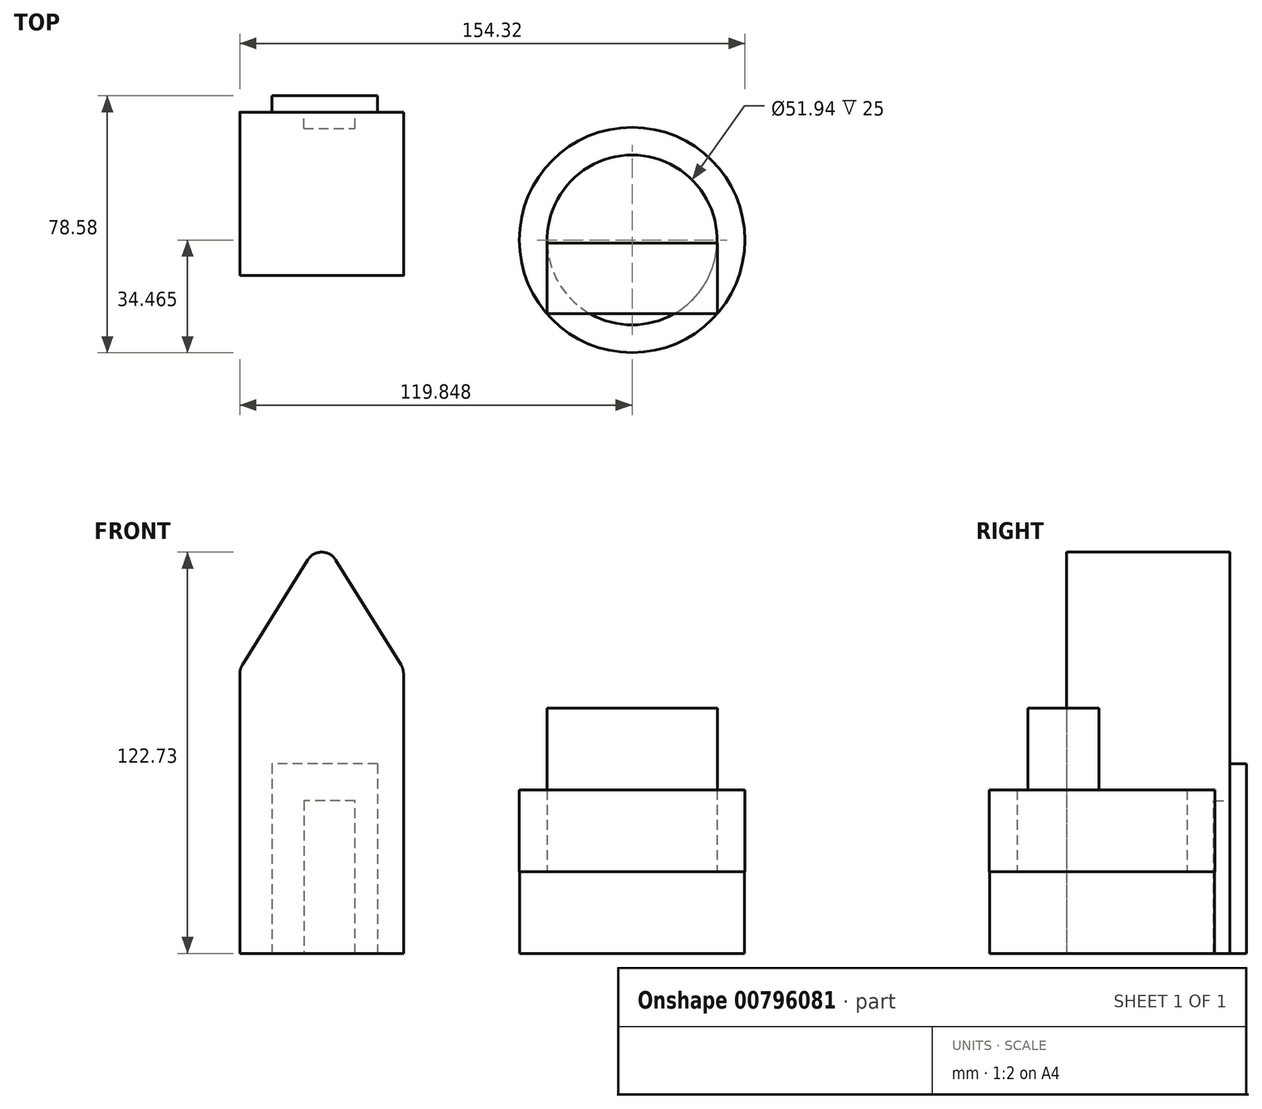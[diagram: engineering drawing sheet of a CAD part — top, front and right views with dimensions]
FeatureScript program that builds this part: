
annotation { "Feature Type Name" : "Feature", "Feature Type Description" : "" }
export const myFeature = defineFeature(function(context is Context, id is Id, definition is map)
    precondition{}
    {
        {
            var Q0;
            Q0=qCreatedBy(makeId("Top.planeOp"),FACE);
            var sketch = newSketch(context, id + "F0", { "sketchPlane" : qUnion([Q0])});
            skPoint(sketch, "E0.middle", {"position": v(0, 0) * mm});
            skLineSegment(sketch, "E1.bottom", {"start": v(-19.52, 23.08) * mm, "end": v(30.48, 23.08) * mm});
            skLineSegment(sketch, "E1.top", {"start": v(-19.52, -26.92) * mm, "end": v(30.48, -26.92) * mm});
            skLineSegment(sketch, "E1.left", {"start": v(-19.52, 23.08) * mm, "end": v(-19.52, -26.92) * mm});
            skLineSegment(sketch, "E1.right", {"start": v(30.48, 23.08) * mm, "end": v(30.48, -26.92) * mm});
            skSolve(sketch);
        }
        {
            var Q0;
            Q0 = qSketchRegion(id + "F0", true);
            extrude(context, id + "F1", {"entities" : qUnion([Q0]), "depth" : 87 * mm, "offsetDistance" : 25 * mm});
        }
        {
            var Q0;
            Q0=makeQuery(id+"F1.opExtrude","SWEPT_FACE",FACE,{"disambiguationData":[OSD([sQuery(id+"F0.wireOp",EDGE,"E1.bottom")])]});
            var sketch = newSketch(context, id + "F2", { "sketchPlane" : qUnion([Q0])});
            skLineSegment(sketch, "E2", {"start": v(-30.48, 87) * mm, "end": v(-5.48, 127.2) * mm});
            skPoint(sketch, "E2.endSnap0", {"position": v(-5.48, 0) * mm});
            skLineSegment(sketch, "E3", {"start": v(-5.48, 127.2) * mm, "end": v(19.52, 87) * mm});
            skLineSegment(sketch, "E4", {"start": v(19.52, 87) * mm, "end": v(-30.48, 87) * mm});
            skSolve(sketch);
        }
        {
            var Q0;
            Q0 = qSketchRegion(id + "F2", true);
            extrude(context, id + "F3", {"entities" : qUnion([Q0]), "operationType" : NewBodyOperationType.ADD, "oppositeDirection" : true, "depth" : 50 * mm, "offsetDistance" : 25 * mm});
        }
        {
            var Q0;
            Q0=makeQuery(id+"F3.boolean.opBoolean","MERGE",FACE,{"derivedFrom":[makeQuery(id+"F1.opExtrude","SWEPT_FACE",FACE,{"disambiguationData":[OSD([sQuery(id+"F0.wireOp",EDGE,"E1.bottom")])]}),makeQuery(id+"F3.opExtrude","CAP_FACE",FACE,{"disambiguationData":[OSD([sQuery(id+"F2.wireOp",EDGE,"E2"),sQuery(id+"F2.wireOp",EDGE,"E3"),sQuery(id+"F2.wireOp",EDGE,"E4")])],"isStart":true})]});
            var sketch = newSketch(context, id + "F4", { "sketchPlane" : qUnion([Q0])});
            skLineSegment(sketch, "E5", {"start": v(-15.66, 0) * mm, "end": v(-15.66, 46.7) * mm});
            skLineSegment(sketch, "E6", {"start": v(-15.66, 46.7) * mm, "end": v(0, 46.7) * mm});
            skLineSegment(sketch, "E7", {"start": v(0, 46.7) * mm, "end": v(0, 0) * mm});
            skLineSegment(sketch, "E8", {"start": v(0, 0) * mm, "end": v(-15.66, 0) * mm});
            skSolve(sketch);
        }
        {
            var Q0;
            Q0 = qSketchRegion(id + "F4", true);
            extrude(context, id + "F5", {"entities" : qUnion([Q0]), "operationType" : NewBodyOperationType.REMOVE, "oppositeDirection" : true, "depth" : 5 * mm, "offsetDistance" : 25 * mm});
        }
        {
            var Q0;
            Q0=makeQuery(id+"F3.boolean.opBoolean","MERGE",FACE,{"derivedFrom":[makeQuery(id+"F1.opExtrude","SWEPT_FACE",FACE,{"disambiguationData":[OSD([sQuery(id+"F0.wireOp",EDGE,"E1.bottom")])]}),makeQuery(id+"F3.opExtrude","CAP_FACE",FACE,{"disambiguationData":[OSD([sQuery(id+"F2.wireOp",EDGE,"E2"),sQuery(id+"F2.wireOp",EDGE,"E3"),sQuery(id+"F2.wireOp",EDGE,"E4")])],"isStart":true})]});
            var sketch = newSketch(context, id + "F6", { "sketchPlane" : qUnion([Q0])});
            skLineSegment(sketch, "E9.bottom", {"start": v(-22.6, 57.96) * mm, "end": v(9.76, 57.96) * mm});
            skLineSegment(sketch, "E9.top", {"start": v(-22.6, 0) * mm, "end": v(9.76, 0) * mm});
            skLineSegment(sketch, "E9.left", {"start": v(-22.6, 57.96) * mm, "end": v(-22.6, 0) * mm});
            skLineSegment(sketch, "E9.right", {"start": v(9.76, 57.96) * mm, "end": v(9.76, 0) * mm});
            skSolve(sketch);
        }
        {
            var Q0;
            Q0 = qSketchRegion(id + "F6", true);
            extrude(context, id + "F7", {"entities" : qUnion([Q0]), "operationType" : NewBodyOperationType.ADD, "depth" : 5 * mm, "offsetDistance" : 25 * mm});
        }
        {
            var Q0;
            Q0=makeQuery(id+"F3.opExtrude","SWEPT_EDGE",EDGE,{"disambiguationData":[OSD([sQuery(id+"F2.wireOp",EDGE,"E2"),sQuery(id+"F2.wireOp",EDGE,"E3")])]});
            var Q1;
            {var subQ0=sQuery(id+"F0.wireOp",EDGE,"E1.right");Q1=makeQuery(id+"F3.boolean.opBoolean","MERGE",EDGE,{"derivedFrom":[makeQuery(id+"F1.opExtrude","CAP_EDGE",EDGE,{"disambiguationData":[OSD([subQ0])],"isStart":false}),makeQuery(id+"F3.opExtrude","SWEPT_EDGE",EDGE,{"disambiguationData":[OSD([sQuery(id+"F0.wireOp",EDGE,"E1.bottom"),subQ0,sQuery(id+"F2.wireOp",EDGE,"E2"),sQuery(id+"F2.wireOp",EDGE,"E4")])]})]});}
            var Q2;
            {var subQ0=sQuery(id+"F0.wireOp",EDGE,"E1.left");Q2=makeQuery(id+"F3.boolean.opBoolean","MERGE",EDGE,{"derivedFrom":[makeQuery(id+"F1.opExtrude","CAP_EDGE",EDGE,{"disambiguationData":[OSD([subQ0])],"isStart":false}),makeQuery(id+"F3.opExtrude","SWEPT_EDGE",EDGE,{"disambiguationData":[OSD([sQuery(id+"F0.wireOp",EDGE,"E1.bottom"),subQ0,sQuery(id+"F2.wireOp",EDGE,"E3"),sQuery(id+"F2.wireOp",EDGE,"E4")])]})]});}
            fillet(context, id + "F8", {"entities" : qUnion([Q0, Q1, Q2]), "radius" : 5 * mm, "tangentPropagation" : true, "allowEdgeOverflow" : false});
        }
        {
            var Q0;
            Q0=qCreatedBy(makeId("Top.planeOp"),FACE);
            var sketch = newSketch(context, id + "F9", { "sketchPlane" : qUnion([Q0])});
            skCircle(sketch, "E10", {"center": v(100.33, -16.04) * mm, "radius": 34.38 * mm});
            skSolve(sketch);
        }
        {
            var Q0;
            Q0 = qSketchRegion(id + "F9", true);
            extrude(context, id + "F10", {"entities" : qUnion([Q0]), "depth" : 25 * mm, "offsetDistance" : 25 * mm});
        }
        {
            var Q0;
            Q0=makeQuery(id+"F10.opExtrude","CAP_FACE",FACE,{"disambiguationData":[OSD([sQuery(id+"F9.wireOp",EDGE,"E10")])],"isStart":false});
            var sketch = newSketch(context, id + "F11", { "sketchPlane" : qUnion([Q0])});
            skCircle(sketch, "E11", {"center": v(100.33, -16.04) * mm, "radius": 34.47 * mm});
            skCircle(sketch, "E12", {"center": v(100.33, -16.04) * mm, "radius": 25.97 * mm});
            skSolve(sketch);
        }
        {
            var Q0;
            Q0 = qSketchRegion(id + "F11", true);
            extrude(context, id + "F12", {"entities" : qUnion([Q0]), "operationType" : NewBodyOperationType.ADD, "depth" : 25 * mm, "offsetDistance" : 25 * mm});
        }
        {
            var Q0;
            Q0=makeQuery(id+"F12.opExtrude","CAP_FACE",FACE,{"disambiguationData":[OSD([sQuery(id+"F11.wireOp",EDGE,"E11"),sQuery(id+"F11.wireOp",EDGE,"E12")])],"isStart":false});
            var sketch = newSketch(context, id + "F13", { "sketchPlane" : qUnion([Q0])});
            skLineSegment(sketch, "E13.bottom", {"start": v(74.37, -17) * mm, "end": v(126.35, -17) * mm});
            skLineSegment(sketch, "E13.top", {"start": v(74.37, -38.63) * mm, "end": v(126.35, -38.63) * mm});
            skLineSegment(sketch, "E13.left", {"start": v(74.37, -17) * mm, "end": v(74.37, -38.63) * mm});
            skLineSegment(sketch, "E13.right", {"start": v(126.35, -17) * mm, "end": v(126.35, -38.63) * mm});
            skSolve(sketch);
        }
        {
            var Q0;
            Q0 = qSketchRegion(id + "F13", true);
            extrude(context, id + "F14", {"entities" : qUnion([Q0]), "operationType" : NewBodyOperationType.ADD, "depth" : 25 * mm, "offsetDistance" : 25 * mm});
        }
    });
